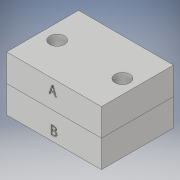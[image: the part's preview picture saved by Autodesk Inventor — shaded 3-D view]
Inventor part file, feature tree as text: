
AUTODESK INVENTOR PART (.ipt)
format: ipt  version: 2019.3 (Build 233278000, 278)  size: 333,824 bytes
history: native  units: mm
features: sketch x5, other x4, extrude x3, fillet x2, revolve x1, pattern_linear x1, emboss x1, hole x1, boolean_combine x1, split x1
ambient origin geometry x8: Origin, YZ Plane, XZ Plane, XY Plane, X Axis, Y Axis, Z Axis, Center Point
bodies: Body1 (feature_tree), Body2 (feature_tree)
feature tree (20):
  other  "Cap"
  sketch  "Sketch1"  dims[d0=15.875mm d1=14.0mm]
  extrude  "Extrusion1"  Depth=14.0mm
  extrude  "Extrusion2"  Depth=17.75mm TaperAngle=0.0deg
  revolve  "Revolution2"  [1 undecoded]
  fillet  "Fillet1"  Radius=30.0mm
  pattern_linear  "Rectangular Pattern1"  Spacing1=18.75mm  [1 undecoded]
  fillet  "Fillet2"  Radius=0.5mm
  extrude  "Extrusion3"  [1 undecoded]
  emboss  "Emboss1"
  hole  "Hole1"  [1 undecoded]
  boolean_combine  "Combine1"
  split  "Split1"
  sketch  "Sketch2"  dims[d2=3.0mm d3=0.0mm d4=17.75mm d5=0.0mm]
  sketch  "Sketch3"  dims[d7=90.0deg d9=2.0mm d10=30.0mm d12=4.0mm]
  other  "Mould"
  sketch  "Sketch4"  dims[d13=0.5mm]
  sketch  "Sketch6"  dims[d14=2.0mm d15=18.75mm d16=0.0mm d18=5.1mm d19=6.0mm d20=4.0mm d21=2.0mm d22=90.0deg d23=8.0mm d24=20.594885mm d25=0.5mm d26=0.0mm]
  other  "5_8-Cap-MoldA"
  other  "5_8-Cap-MoldB"
note: 4 required parameter values undecoded (feature->parameter linkage not recoverable at this tier; creation-order binding heuristic only, values carry confidence <= 0.55)